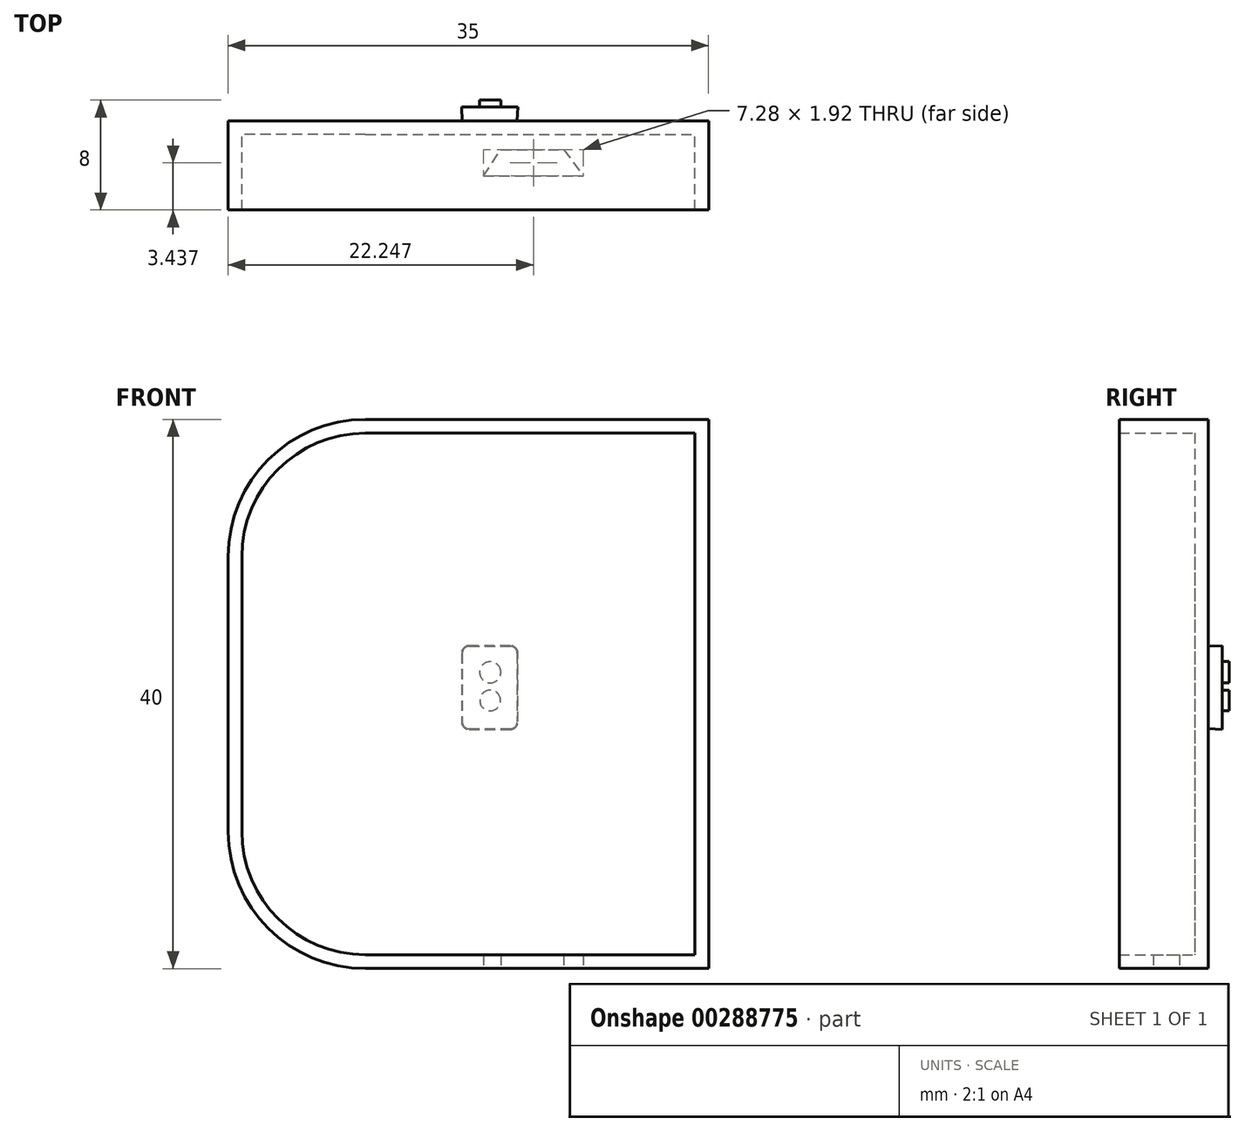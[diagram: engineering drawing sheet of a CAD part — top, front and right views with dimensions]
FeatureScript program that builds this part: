
annotation { "Feature Type Name" : "Feature", "Feature Type Description" : "" }
export const myFeature = defineFeature(function(context is Context, id is Id, definition is map)
    precondition{}
    {
        {
            var Q0;
            Q0=qCreatedBy(makeId("Front.planeOp"),FACE);
            var sketch = newSketch(context, id + "F0", { "sketchPlane" : qUnion([Q0])});
            skLineSegment(sketch, "E0.bottom", {"start": v(-47.96, 57.83) * mm, "end": v(-22.96, 57.83) * mm});
            skLineSegment(sketch, "E0.top", {"start": v(-47.96, 17.83) * mm, "end": v(-22.96, 17.83) * mm});
            skLineSegment(sketch, "E0.left", {"start": v(-57.96, 47.83) * mm, "end": v(-57.96, 27.83) * mm});
            skLineSegment(sketch, "E0.right", {"start": v(-22.96, 57.83) * mm, "end": v(-22.96, 17.83) * mm});
            skPoint(sketch, "E1.visualSharp", {"position": v(-57.96, 57.83) * mm});
            skArc(sketch, "E1.filletArc", {"start": v(-47.96, 57.83) * mm, "mid": v(-55.03, 54.9) * mm, "end": v(-57.96, 47.83) * mm});
            skPoint(sketch, "E2.visualSharp", {"position": v(-57.96, 17.83) * mm});
            skArc(sketch, "E2.filletArc", {"start": v(-57.96, 27.83) * mm, "mid": v(-55.03, 20.76) * mm, "end": v(-47.96, 17.83) * mm});
            skSolve(sketch);
        }
        {
            var Q0;
            Q0 = qSketchRegion(id + "F0", true);
            extrude(context, id + "F1", {"entities" : qUnion([Q0]), "depth" : 6.5 * mm});
        }
        {
            var Q0;
            Q0=makeQuery(id+"F1.opExtrude","CAP_FACE",FACE,{"disambiguationData":[OSD([sQuery(id+"F0.wireOp",EDGE,"E0.bottom"),sQuery(id+"F0.wireOp",EDGE,"E0.top"),sQuery(id+"F0.wireOp",EDGE,"E0.left"),sQuery(id+"F0.wireOp",EDGE,"E0.right"),sQuery(id+"F0.wireOp",EDGE,"E1.filletArc"),sQuery(id+"F0.wireOp",EDGE,"E2.filletArc")])],"isStart":false});
            shell(context, id + "F2", {"entities" : qUnion([Q0]), "thickness" : 1 * mm});
        }
        {
            var Q0;
            Q0=makeQuery(id+"F1.opExtrude","SWEPT_FACE",FACE,{"disambiguationData":[OSD([sQuery(id+"F0.wireOp",EDGE,"E0.top")])]});
            var sketch = newSketch(context, id + "F3", { "sketchPlane" : qUnion([Q0])});
            skLineSegment(sketch, "E3.bottom", {"start": v(-39.35, 4.02) * mm, "end": v(-32.07, 4.02) * mm});
            skLineSegment(sketch, "E3.top", {"start": v(-39.35, 2.1) * mm, "end": v(-32.07, 2.1) * mm});
            skLineSegment(sketch, "E3.left", {"start": v(-39.35, 4.02) * mm, "end": v(-39.35, 2.1) * mm});
            skLineSegment(sketch, "E3.right", {"start": v(-32.07, 4.02) * mm, "end": v(-32.07, 2.1) * mm});
            skLineSegment(sketch, "E4", {"start": v(-39.35, 4.02) * mm, "end": v(-38.09, 2.1) * mm});
            skLineSegment(sketch, "E5", {"start": v(-38.09, 2.1) * mm, "end": v(-33.5, 2.1) * mm});
            skLineSegment(sketch, "E6", {"start": v(-33.5, 2.1) * mm, "end": v(-32.07, 4.02) * mm});
            skSolve(sketch);
        }
        {
            var Q0;
            Q0=makeQuery(id+"F3.imprint","IMPRINT",FACE,{"disambiguationData":[TD([[makeQuery(id+"F3.imprint","IMPRINT",EDGE,{"derivedFrom":sQuery(id+"F3.wireOp",EDGE,"E3.bottom")}),-1.0]])]});
            extrude(context, id + "F4", {"entities" : qUnion([Q0]), "operationType" : NewBodyOperationType.REMOVE, "oppositeDirection" : true, "depth" : 25 * mm});
        }
        {
            var Q0;
            Q0=makeQuery(id+"F1.opExtrude","CAP_FACE",FACE,{"disambiguationData":[OSD([sQuery(id+"F0.wireOp",EDGE,"E0.bottom"),sQuery(id+"F0.wireOp",EDGE,"E0.top"),sQuery(id+"F0.wireOp",EDGE,"E0.left"),sQuery(id+"F0.wireOp",EDGE,"E0.right"),sQuery(id+"F0.wireOp",EDGE,"E1.filletArc"),sQuery(id+"F0.wireOp",EDGE,"E2.filletArc")])],"isStart":true});
            var sketch = newSketch(context, id + "F5", { "sketchPlane" : qUnion([Q0])});
            skPoint(sketch, "E7.middle", {"position": v(38.9, 38.3) * mm});
            skLineSegment(sketch, "E8.bottom", {"start": v(40.4, 41.3) * mm, "end": v(37.4, 41.3) * mm});
            skLineSegment(sketch, "E8.top", {"start": v(40.4, 35.3) * mm, "end": v(37.4, 35.3) * mm});
            skLineSegment(sketch, "E8.left", {"start": v(40.9, 40.8) * mm, "end": v(40.9, 35.8) * mm});
            skLineSegment(sketch, "E8.right", {"start": v(36.9, 40.8) * mm, "end": v(36.9, 35.8) * mm});
            skPoint(sketch, "E9.visualSharp", {"position": v(36.9, 41.3) * mm});
            skArc(sketch, "E9.filletArc", {"start": v(37.4, 41.3) * mm, "mid": v(37.05, 41.16) * mm, "end": v(36.9, 40.8) * mm});
            skPoint(sketch, "E10.visualSharp", {"position": v(40.9, 41.3) * mm});
            skArc(sketch, "E10.filletArc", {"start": v(40.9, 40.8) * mm, "mid": v(40.76, 41.16) * mm, "end": v(40.4, 41.3) * mm});
            skPoint(sketch, "E11.visualSharp", {"position": v(40.9, 35.3) * mm});
            skArc(sketch, "E11.filletArc", {"start": v(40.4, 35.3) * mm, "mid": v(40.76, 35.45) * mm, "end": v(40.9, 35.8) * mm});
            skPoint(sketch, "E12.visualSharp", {"position": v(36.9, 35.3) * mm});
            skArc(sketch, "E12.filletArc", {"start": v(36.9, 35.8) * mm, "mid": v(37.05, 35.45) * mm, "end": v(37.4, 35.3) * mm});
            skSolve(sketch);
        }
        {
            var Q0;
            Q0 = qSketchRegion(id + "F5", true);
            extrude(context, id + "F6", {"entities" : qUnion([Q0]), "operationType" : NewBodyOperationType.ADD, "depth" : 1 * mm, "hasDraft" : true, "draftAngle" : 3 * degree, "hasSecondDirection" : true, "secondDirectionOppositeDirection" : true, "secondDirectionDepth" : 1 * mm});
        }
        {
            var Q0;
            Q0=makeQuery(id+"F6.opExtrude","CAP_FACE",FACE,{"disambiguationData":[OSD([sQuery(id+"F5.wireOp",EDGE,"E8.bottom"),sQuery(id+"F5.wireOp",EDGE,"E8.top"),sQuery(id+"F5.wireOp",EDGE,"E8.left"),sQuery(id+"F5.wireOp",EDGE,"E8.right"),sQuery(id+"F5.wireOp",EDGE,"E9.filletArc"),sQuery(id+"F5.wireOp",EDGE,"E10.filletArc"),sQuery(id+"F5.wireOp",EDGE,"E11.filletArc"),sQuery(id+"F5.wireOp",EDGE,"E12.filletArc")])],"isStart":false});
            var sketch = newSketch(context, id + "F7", { "sketchPlane" : qUnion([Q0])});
            skSolve(sketch);
        }
        {
            var Q0;
            Q0=makeQuery(id+"F7.imprint","IMPRINT",FACE,{"disambiguationData":[TD([[makeQuery(id+"F7.imprint","IMPRINT",EDGE,{"derivedFrom":makeQuery(id+"F6.opExtrude","CAP_EDGE",EDGE,{"disambiguationData":[OSD([sQuery(id+"F5.wireOp",EDGE,"E8.bottom")])],"isStart":false})}),1.0]])]});
            var sketch = newSketch(context, id + "F8", { "sketchPlane" : qUnion([Q0])});
            skCircle(sketch, "E13", {"center": v(38.86, 39.41) * mm, "radius": 0.77 * mm});
            skCircle(sketch, "E14", {"center": v(38.86, 37.36) * mm, "radius": 0.76 * mm});
            skSolve(sketch);
        }
        {
            var Q0;
            Q0 = qSketchRegion(id + "F8", true);
            extrude(context, id + "F9", {"entities" : qUnion([Q0]), "depth" : 0.5 * mm});
        }
    });
